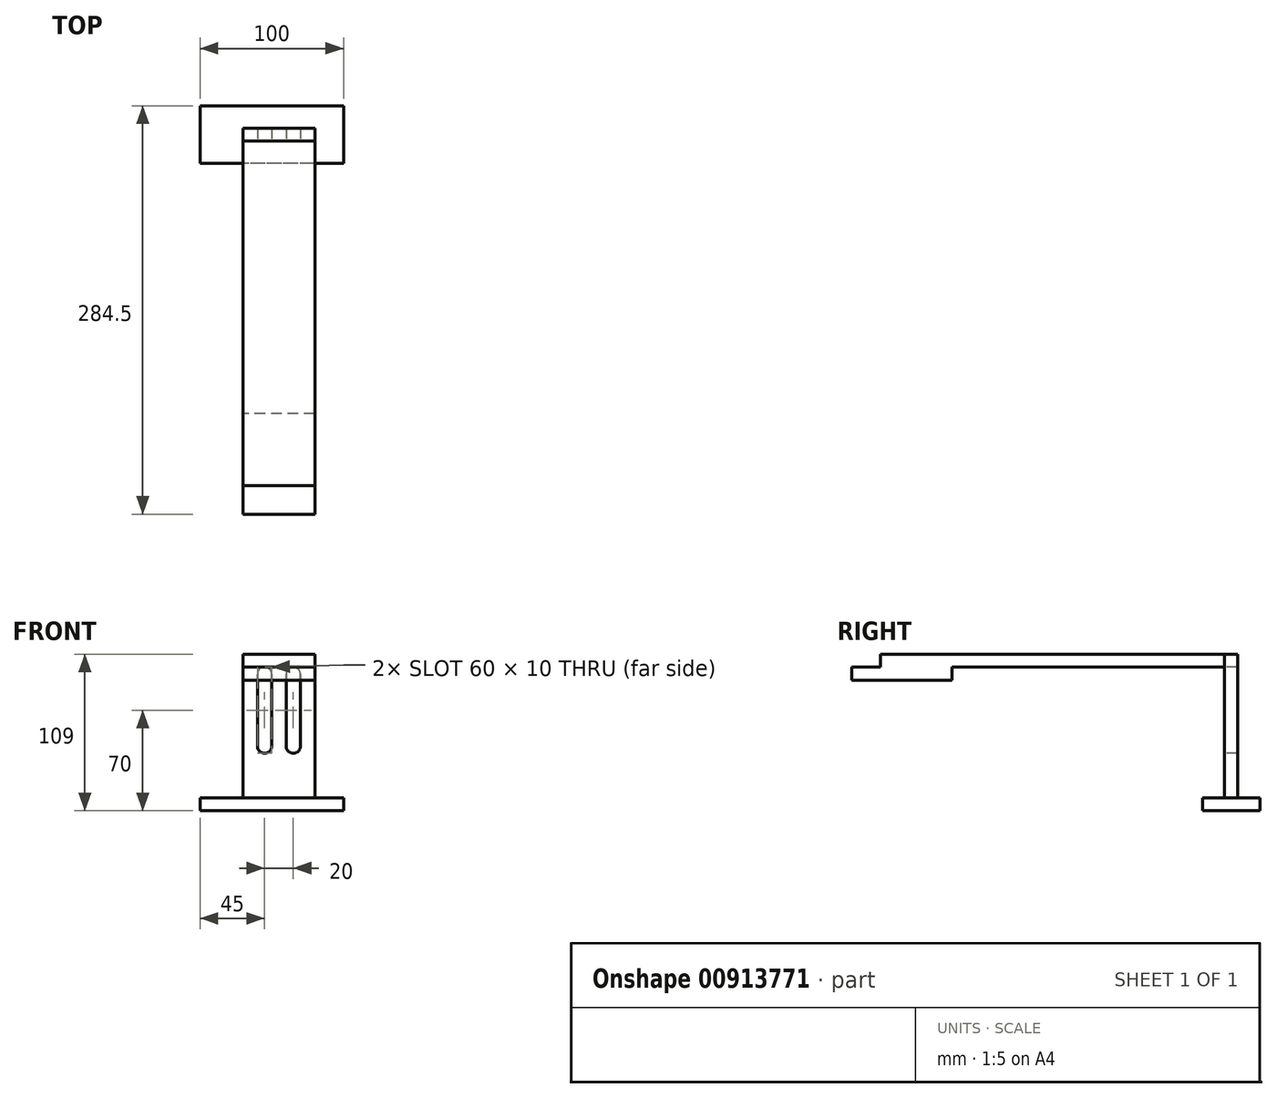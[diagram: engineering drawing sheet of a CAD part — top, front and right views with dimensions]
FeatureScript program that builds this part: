
annotation { "Feature Type Name" : "Feature", "Feature Type Description" : "" }
export const myFeature = defineFeature(function(context is Context, id is Id, definition is map)
    precondition{}
    {
        {
            var Q0;
            Q0=qCreatedBy(makeId("Top.planeOp"),FACE);
            var sketch = newSketch(context, id + "F0", { "sketchPlane" : qUnion([Q0])});
            skLineSegment(sketch, "E0.bottom", {"start": v(50, 20) * mm, "end": v(-50, 20) * mm});
            skLineSegment(sketch, "E0.top", {"start": v(50, -20) * mm, "end": v(-50, -20) * mm});
            skLineSegment(sketch, "E0.left", {"start": v(50, 20) * mm, "end": v(50, -20) * mm});
            skLineSegment(sketch, "E0.right", {"start": v(-50, 20) * mm, "end": v(-50, -20) * mm});
            skPoint(sketch, "E0.middle", {"position": v(0, 0) * mm});
            skSolve(sketch);
        }
        {
            var Q0;
            Q0=makeQuery(id+"F0.imprint","IMPRINT",FACE,{"disambiguationData":[TD([[makeQuery(id+"F0.imprint","IMPRINT",EDGE,{"derivedFrom":sQuery(id+"F0.wireOp",EDGE,"E0.bottom")}),1.0]])]});
            extrude(context, id + "F1", {"entities" : qUnion([Q0]), "depth" : 9 * mm, "offsetDistance" : 25 * mm});
        }
        {
            var Q0;
            Q0=makeQuery(id+"F1.opExtrude","CAP_FACE",FACE,{"disambiguationData":[OSD([sQuery(id+"F0.wireOp",EDGE,"E0.bottom"),sQuery(id+"F0.wireOp",EDGE,"E0.top"),sQuery(id+"F0.wireOp",EDGE,"E0.left"),sQuery(id+"F0.wireOp",EDGE,"E0.right")])],"isStart":false});
            var sketch = newSketch(context, id + "F2", { "sketchPlane" : qUnion([Q0])});
            skLineSegment(sketch, "E1.bottom", {"start": v(-20, -4.5) * mm, "end": v(30, -4.5) * mm});
            skLineSegment(sketch, "E1.top", {"start": v(-20, 4.5) * mm, "end": v(30, 4.5) * mm});
            skLineSegment(sketch, "E1.left", {"start": v(-20, -4.5) * mm, "end": v(-20, 4.5) * mm});
            skLineSegment(sketch, "E1.right", {"start": v(30, -4.5) * mm, "end": v(30, 4.5) * mm});
            skPoint(sketch, "E1.middle", {"position": v(5, 0) * mm});
            skSolve(sketch);
        }
        {
            var Q0;
            Q0 = qSketchRegion(id + "F2", true);
            extrude(context, id + "F3", {"entities" : qUnion([Q0]), "operationType" : NewBodyOperationType.ADD, "depth" : 100 * mm, "offsetDistance" : 25 * mm});
        }
        {
            var Q0;
            Q0=makeQuery(id+"F3.opExtrude","SWEPT_FACE",FACE,{"disambiguationData":[OSD([sQuery(id+"F2.wireOp",EDGE,"E1.bottom")])]});
            var sketch = newSketch(context, id + "F4", { "sketchPlane" : qUnion([Q0])});
            skLineSegment(sketch, "E2.bottom", {"start": v(-5, 100) * mm, "end": v(-5, 100) * mm});
            skLineSegment(sketch, "E2.top", {"start": v(-5, 40) * mm, "end": v(-5, 40) * mm});
            skLineSegment(sketch, "E2.left", {"start": v(-10, 95) * mm, "end": v(-10, 45) * mm});
            skLineSegment(sketch, "E2.right", {"start": v(0, 95) * mm, "end": v(0, 45) * mm});
            skLineSegment(sketch, "E3.bottom", {"start": v(15, 100) * mm, "end": v(15, 100) * mm});
            skLineSegment(sketch, "E3.top", {"start": v(15, 40) * mm, "end": v(15, 40) * mm});
            skLineSegment(sketch, "E3.left", {"start": v(10, 95) * mm, "end": v(10, 45) * mm});
            skLineSegment(sketch, "E3.right", {"start": v(20, 95) * mm, "end": v(20, 45) * mm});
            skPoint(sketch, "E4.visualSharp", {"position": v(-10, 100) * mm});
            skArc(sketch, "E4.filletArc", {"start": v(-5, 100) * mm, "mid": v(-8.54, 98.54) * mm, "end": v(-10, 95) * mm});
            skPoint(sketch, "E5.visualSharp", {"position": v(0, 100) * mm});
            skArc(sketch, "E5.filletArc", {"start": v(0, 95) * mm, "mid": v(-1.46, 98.54) * mm, "end": v(-5, 100) * mm});
            skPoint(sketch, "E6.visualSharp", {"position": v(-10, 40) * mm});
            skArc(sketch, "E6.filletArc", {"start": v(-10, 45) * mm, "mid": v(-8.54, 41.46) * mm, "end": v(-5, 40) * mm});
            skPoint(sketch, "E7.visualSharp", {"position": v(0, 40) * mm});
            skArc(sketch, "E7.filletArc", {"start": v(-5, 40) * mm, "mid": v(-1.46, 41.46) * mm, "end": v(0, 45) * mm});
            skPoint(sketch, "E8.visualSharp", {"position": v(10, 40) * mm});
            skArc(sketch, "E8.filletArc", {"start": v(10, 45) * mm, "mid": v(11.46, 41.46) * mm, "end": v(15, 40) * mm});
            skPoint(sketch, "E9.visualSharp", {"position": v(20, 40) * mm});
            skArc(sketch, "E9.filletArc", {"start": v(15, 40) * mm, "mid": v(18.54, 41.46) * mm, "end": v(20, 45) * mm});
            skPoint(sketch, "E10.visualSharp", {"position": v(10, 100) * mm});
            skArc(sketch, "E10.filletArc", {"start": v(15, 100) * mm, "mid": v(11.46, 98.54) * mm, "end": v(10, 95) * mm});
            skPoint(sketch, "E11.visualSharp", {"position": v(20, 100) * mm});
            skArc(sketch, "E11.filletArc", {"start": v(20, 95) * mm, "mid": v(18.54, 98.54) * mm, "end": v(15, 100) * mm});
            skSolve(sketch);
        }
        {
            var Q0;
            Q0 = qSketchRegion(id + "F4", true);
            extrude(context, id + "F5", {"entities" : qUnion([Q0]), "operationType" : NewBodyOperationType.REMOVE, "oppositeDirection" : true, "depth" : 18 * mm, "offsetDistance" : 25 * mm});
        }
        {
            var Q0;
            Q0=makeQuery(id+"F3.opExtrude","SWEPT_FACE",FACE,{"disambiguationData":[OSD([sQuery(id+"F2.wireOp",EDGE,"E1.bottom")])]});
            var sketch = newSketch(context, id + "F6", { "sketchPlane" : qUnion([Q0])});
            skLineSegment(sketch, "E12.bottom", {"start": v(30, 109) * mm, "end": v(-20, 109) * mm});
            skLineSegment(sketch, "E12.top", {"start": v(30, 100) * mm, "end": v(-20, 100) * mm});
            skLineSegment(sketch, "E12.left", {"start": v(30, 109) * mm, "end": v(30, 100) * mm});
            skLineSegment(sketch, "E12.right", {"start": v(-20, 109) * mm, "end": v(-20, 100) * mm});
            skSolve(sketch);
        }
        {
            var Q0;
            Q0=makeQuery(id+"F6.imprint","IMPRINT",FACE,{"disambiguationData":[TD([[makeQuery(id+"F6.imprint","IMPRINT",EDGE,{"derivedFrom":sQuery(id+"F6.wireOp",EDGE,"E12.bottom")}),-1.0]])]});
            extrude(context, id + "F7", {"entities" : qUnion([Q0]), "depth" : 240 * mm, "offsetDistance" : 25 * mm});
        }
        {
            var Q0;
            Q0=makeQuery(id+"F7.opExtrude","SWEPT_FACE",FACE,{"disambiguationData":[OSD([sQuery(id+"F6.wireOp",EDGE,"E12.top")])]});
            var sketch = newSketch(context, id + "F8", { "sketchPlane" : qUnion([Q0])});
            skLineSegment(sketch, "E13.bottom", {"start": v(30, 244.5) * mm, "end": v(-20, 244.5) * mm});
            skLineSegment(sketch, "E13.top", {"start": v(30, 194.5) * mm, "end": v(-20, 194.5) * mm});
            skLineSegment(sketch, "E13.left", {"start": v(30, 244.5) * mm, "end": v(30, 194.5) * mm});
            skLineSegment(sketch, "E13.right", {"start": v(-20, 244.5) * mm, "end": v(-20, 194.5) * mm});
            skSolve(sketch);
        }
        {
            var Q0;
            Q0 = qSketchRegion(id + "F8", true);
            extrude(context, id + "F9", {"entities" : qUnion([Q0]), "depth" : 9 * mm, "offsetDistance" : 25 * mm});
        }
        {
            var Q0;
            Q0=makeQuery(id+"F9.opExtrude","SWEPT_FACE",FACE,{"disambiguationData":[OSD([sQuery(id+"F8.wireOp",EDGE,"E13.bottom")])]});
            var sketch = newSketch(context, id + "F10", { "sketchPlane" : qUnion([Q0])});
            skLineSegment(sketch, "E14.bottom", {"start": v(30, 100) * mm, "end": v(-20, 100) * mm});
            skLineSegment(sketch, "E14.top", {"start": v(30, 91) * mm, "end": v(-20, 91) * mm});
            skLineSegment(sketch, "E14.left", {"start": v(30, 100) * mm, "end": v(30, 91) * mm});
            skLineSegment(sketch, "E14.right", {"start": v(-20, 100) * mm, "end": v(-20, 91) * mm});
            skSolve(sketch);
        }
        {
            var Q0;
            Q0 = qSketchRegion(id + "F10", true);
            extrude(context, id + "F11", {"entities" : qUnion([Q0]), "operationType" : NewBodyOperationType.ADD, "depth" : 20 * mm, "offsetDistance" : 25 * mm});
        }
    });
